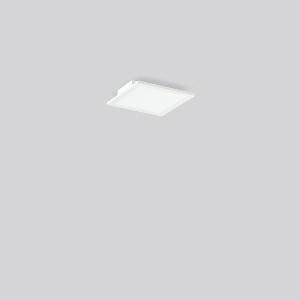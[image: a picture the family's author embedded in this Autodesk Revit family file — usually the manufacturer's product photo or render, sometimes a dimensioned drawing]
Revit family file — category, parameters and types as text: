
# Revit family: sidelite_eco_312375_002_7f18
name_source: partatom
category: Lighting Fixtures
units: mm (PartAtom-declared; Revit-internal decimal feet)

## family parameters
Cut with Voids When Loaded = No
Host = Face
Light Source = No
Part Type = Normal
Room Calculation Point = No
Round Connector Dimension = Use Diameter
Shared = No

## types (1)
- SIDELITE ECO (1 x LED Modul 830, 2100 lm, 3000)
    Apparent Load = 19 VA
    CIE Flux Codes = 47 79 96 100 100
    Color Rendering = 80
    Color Temperature = 3000
    Default Elevation = 1800 mm
    Description = Series: SIDELITE ECO
Highly economical surface mounted luminaire with progressive LED technology. Luminaire frame: aluminium, powder-coated. Mounting frame: sheet steel, powder-coated. Diffuser: plastic, opal. Lightguide and diffuser made of non-yellowing plastic (PMMA). Lateral light emission (RZB SIDELITE technology) for homogeneous light distribution. 
Colour: white
Length: 295 mm
Width: 295 mm
Height: 45.7 mm
Lamp: LED
Socket: without socket
Colour temperature: 3000K
Colour rendering index (CRI): 80
System power: 19 W
Rated luminous flux: 2100 lm
Luminous efficiency: 111 lm/W
Control gear: Regulated power supply
Protection class: II
Type of protection: IP 40
    Height = 46 mm
    Lamp = 1 x LED Modul 830
    Lamp Light Flux = 2100 lm
    Lamp count = 1
    Length = 295 mm
    Lifetime = 50000 h
    Luminous efficacy = 111 lm/W
    Manufacturer = RZB
    ModVariant = No
    Model = 312375.002
    Mounting Place = Ceiling
    Mounting Type = Surface mounted
    Number of Poles = 1
    OnlyDefault = Yes
    Power Factor = 1
    Product Name = SIDELITE ECO
    Product group = Surface mounted modular luminaires
    ProductGroupID = 306
    Protection Class = Protection class II
    Protection Degree = IP 40
    RLX_Detail_Level = 1
    RLX_Emergency_Light_Flux = 0 lm
    RLX_Emergency_Type = 0
    RLX_Emergency_Type_DB = No
    RlxData = <blob elided: 14241 chars, md5=a9a3f127>
    Socket = socket
    Standby Power = 0 W
    System Light Flux = 2100 lm
    System Power = 19 W
    Type Comments = Product without accessories
    Type Image = 312375.002.jpg
    URL = http://relux.com
    VarID = ---
    Voltage = 230 V
    Voltage Range = 220-240 V
    Weight = 0.00 kg
    Width = 295 mm

## geometry (parser evidence)
native form markers: Sweep x11
no freeform markers — native parametric forms only
